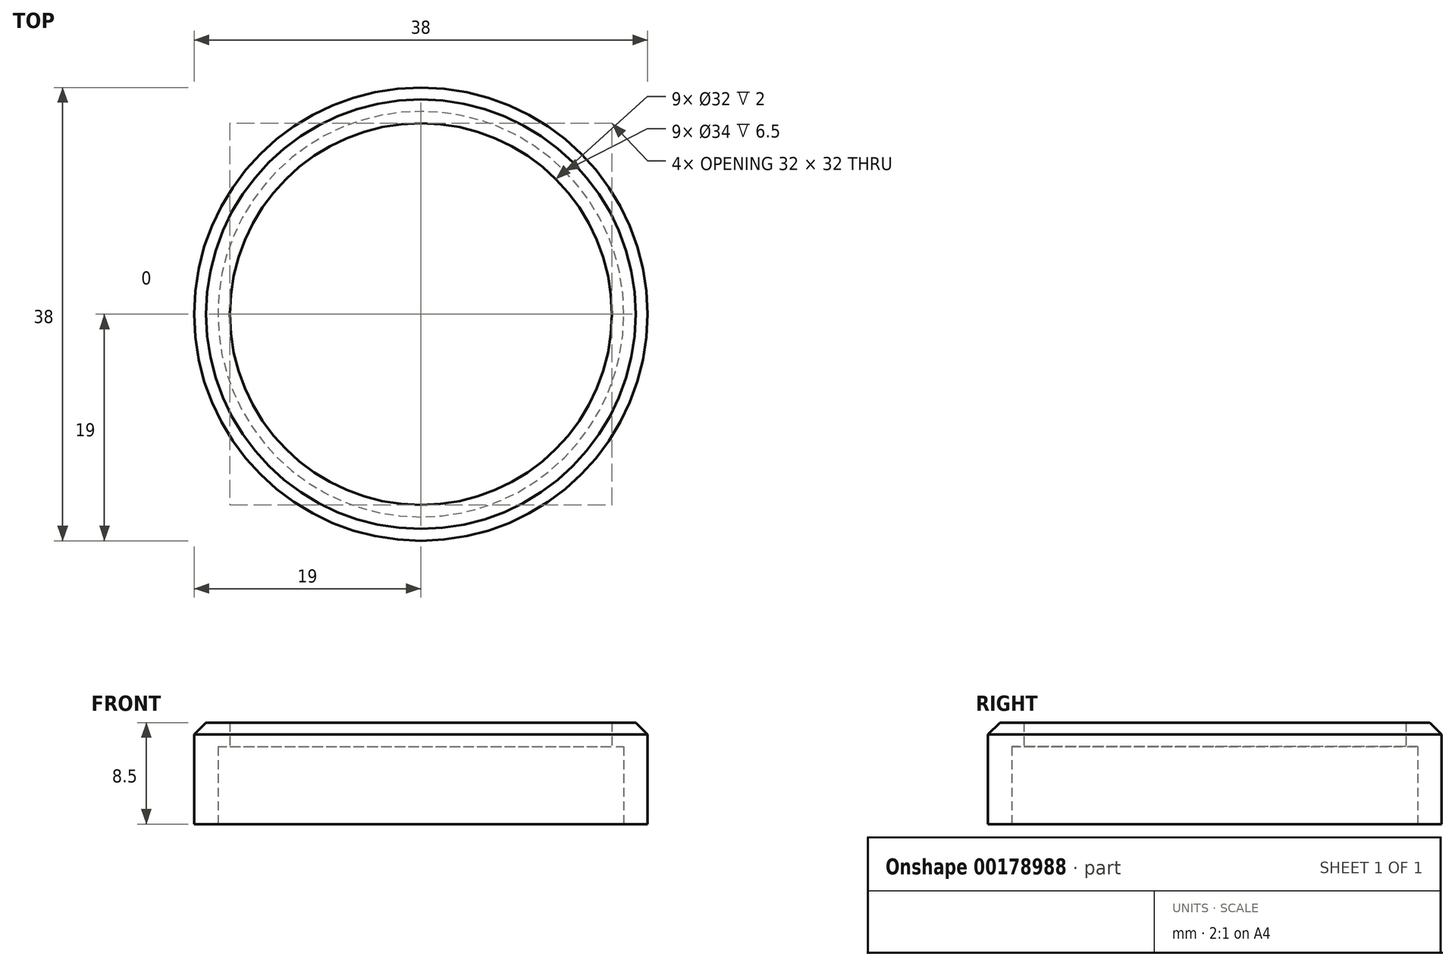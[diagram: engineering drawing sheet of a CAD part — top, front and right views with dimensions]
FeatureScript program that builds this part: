
annotation { "Feature Type Name" : "Feature", "Feature Type Description" : "" }
export const myFeature = defineFeature(function(context is Context, id is Id, definition is map)
    precondition{}
    {
        {
            var Q0;
            Q0=qCreatedBy(makeId("Top.planeOp"),FACE);
            var sketch = newSketch(context, id + "F0", { "sketchPlane" : qUnion([Q0])});
            skCircle(sketch, "E0", {"center": v(0, 0) * mm, "radius": 19 * mm});
            skSolve(sketch);
        }
        {
            var Q0;
            Q0 = qSketchRegion(id + "F0", true);
            extrude(context, id + "F1", {"entities" : qUnion([Q0]), "depth" : 8.5 * mm});
        }
        {
            var Q0;
            Q0=makeQuery(id+"F1.opExtrude","CAP_FACE",FACE,{"disambiguationData":[OSD([sQuery(id+"F0.wireOp",EDGE,"E0")])],"isStart":true});
            var sketch = newSketch(context, id + "F2", { "sketchPlane" : qUnion([Q0])});
            skCircle(sketch, "E1", {"center": v(0, 0) * mm, "radius": 16 * mm});
            skSolve(sketch);
        }
        {
            var Q0;
            Q0 = qSketchRegion(id + "F2", true);
            extrude(context, id + "F3", {"entities" : qUnion([Q0]), "operationType" : NewBodyOperationType.REMOVE, "oppositeDirection" : true, "depth" : 10 * mm});
        }
        {
            var Q0;
            Q0=makeQuery(id+"F1.opExtrude","CAP_FACE",FACE,{"disambiguationData":[OSD([sQuery(id+"F0.wireOp",EDGE,"E0")])],"isStart":true});
            var sketch = newSketch(context, id + "F4", { "sketchPlane" : qUnion([Q0])});
            skCircle(sketch, "E2", {"center": v(0, 0) * mm, "radius": 17 * mm});
            skSolve(sketch);
        }
        {
            var Q0;
            Q0=makeQuery(id+"F4.imprint","IMPRINT",FACE,{"disambiguationData":[TD([[makeQuery(id+"F4.imprint","IMPRINT",EDGE,{"derivedFrom":sQuery(id+"F4.wireOp",EDGE,"E2")}),1.0]])]});
            extrude(context, id + "F5", {"entities" : qUnion([Q0]), "operationType" : NewBodyOperationType.REMOVE, "oppositeDirection" : true, "depth" : 6.5 * mm});
        }
        {
            var Q0;
            Q0=makeQuery(id+"F1.opExtrude","CAP_EDGE",EDGE,{"disambiguationData":[OSD([sQuery(id+"F0.wireOp",EDGE,"E0")])],"isStart":false});
            chamfer(context, id + "F6", {"entities" : qUnion([Q0]), "width" : 1 * mm, "tangentPropagation" : true});
        }
    });
